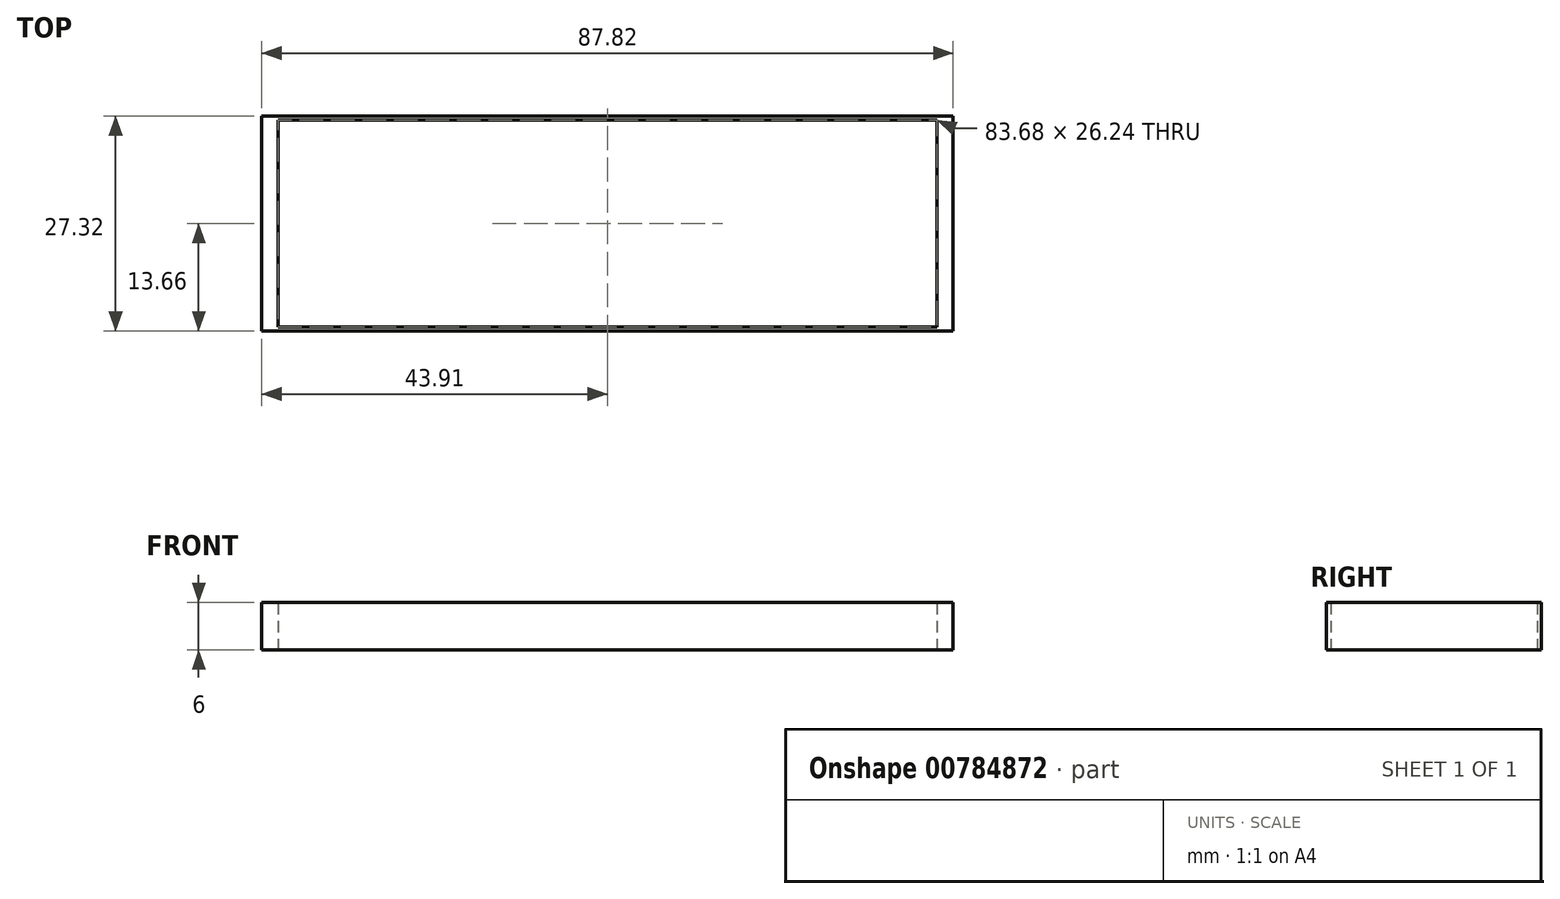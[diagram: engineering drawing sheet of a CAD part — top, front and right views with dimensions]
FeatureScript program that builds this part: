
annotation { "Feature Type Name" : "Feature", "Feature Type Description" : "" }
export const myFeature = defineFeature(function(context is Context, id is Id, definition is map)
    precondition{}
    {
        {
            var Q0;
            Q0=qCreatedBy(makeId("Top.planeOp"),FACE);
            var sketch = newSketch(context, id + "F0", { "sketchPlane" : qUnion([Q0])});
            skLineSegment(sketch, "E0.bottom", {"start": v(43.9, 13.66) * mm, "end": v(-43.9, 13.66) * mm});
            skLineSegment(sketch, "E0.top", {"start": v(43.9, -13.66) * mm, "end": v(-43.9, -13.66) * mm});
            skLineSegment(sketch, "E0.left", {"start": v(43.9, 13.66) * mm, "end": v(43.9, -13.66) * mm});
            skLineSegment(sketch, "E0.right", {"start": v(-43.9, 13.66) * mm, "end": v(-43.9, -13.66) * mm});
            skPoint(sketch, "E0.middle", {"position": v(0, 0) * mm});
            skLineSegment(sketch, "E1.bottom", {"start": v(41.84, 13.12) * mm, "end": v(-41.84, 13.12) * mm});
            skLineSegment(sketch, "E1.top", {"start": v(41.84, -13.12) * mm, "end": v(-41.84, -13.12) * mm});
            skLineSegment(sketch, "E1.left", {"start": v(41.84, 13.12) * mm, "end": v(41.84, -13.12) * mm});
            skLineSegment(sketch, "E1.right", {"start": v(-41.84, 13.12) * mm, "end": v(-41.84, -13.12) * mm});
            skSolve(sketch);
        }
        {
            var Q0;
            Q0 = qSketchRegion(id + "F0", true);
            extrude(context, id + "F1", {"entities" : qUnion([Q0]), "depth" : 6 * mm, "offsetDistance" : 25 * mm});
        }
    });
